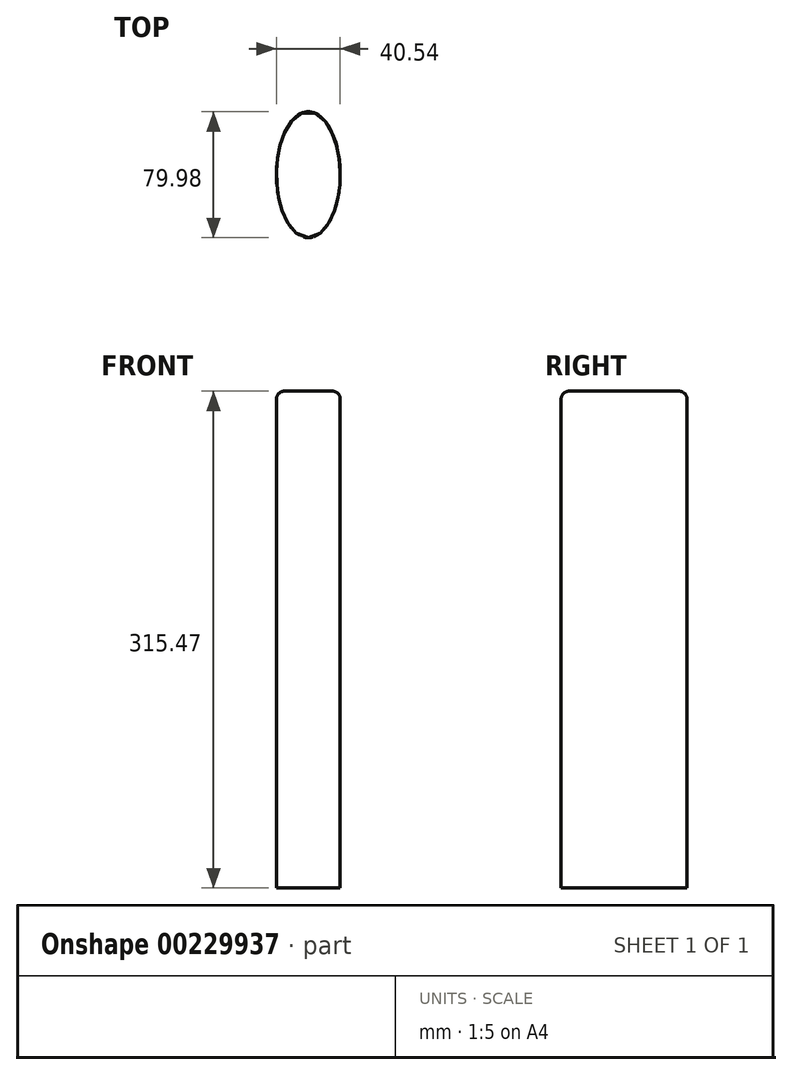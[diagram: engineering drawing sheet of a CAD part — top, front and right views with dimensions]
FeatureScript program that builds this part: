
annotation { "Feature Type Name" : "Feature", "Feature Type Description" : "" }
export const myFeature = defineFeature(function(context is Context, id is Id, definition is map)
    precondition{}
    {
        {
            var Q0;
            Q0=qCreatedBy(makeId("Top.planeOp"),FACE);
            var sketch = newSketch(context, id + "F0", { "sketchPlane" : qUnion([Q0])});
            skEllipse(sketch, "E0", {"center": v(0, 26.92) * mm, "majorRadius": 39.99 * mm, "minorRadius": 20.27 * mm, "majorAxis": v(0, -1)});
            skSolve(sketch);
        }
        {
            var Q0;
            Q0 = qSketchRegion(id + "F0", true);
            extrude(context, id + "F1", {"entities" : qUnion([Q0]), "depth" : 25.4 * mm});
        }
        {
            var Q0;
            Q0=makeQuery(id+"F1.opExtrude","CAP_FACE",FACE,{"disambiguationData":[OSD([sQuery(id+"F0.wireOp",EDGE,"E0")])],"isStart":false});
            var Q1;
            Q1=makeQuery(id+"F1.opExtrude","CAP_FACE",FACE,{"disambiguationData":[OSD([sQuery(id+"F0.wireOp",EDGE,"E0")])],"isStart":true});
            extrude(context, id + "F2", {"entities" : qUnion([Q0, Q1]), "operationType" : NewBodyOperationType.ADD, "depth" : 114.05 * mm});
        }
        {
            var Q0;
            Q0=makeQuery(id+"F1.opExtrude","CAP_FACE",FACE,{"disambiguationData":[OSD([sQuery(id+"F0.wireOp",EDGE,"E0")])],"isStart":true});
            extrude(context, id + "F3", {"entities" : qUnion([Q0]), "operationType" : NewBodyOperationType.ADD, "depth" : 25.4 * mm});
        }
        {
            var Q0;
            Q0=makeQuery(id+"F3.opExtrude","CAP_FACE",FACE,{"disambiguationData":[OSD([sQuery(id+"F0.wireOp",EDGE,"E0")])],"isStart":false});
            extrude(context, id + "F4", {"entities" : qUnion([Q0]), "operationType" : NewBodyOperationType.ADD, "depth" : 150.62 * mm});
        }
        {
            var Q0;
            {var subQ0=sQuery(id+"F0.wireOp",EDGE,"E0");Q0=makeQuery(id+"F2.opExtrude","CAP_EDGE",EDGE,{"disambiguationData":[OSD([subQ0]),TDD([makeQuery(id+"F1.opExtrude","CAP_EDGE",EDGE,{"disambiguationData":[OSD([subQ0])],"isStart":false})])],"isStart":false});}
            fillet(context, id + "F5", {"entities" : qUnion([Q0]), "radius" : 5.08 * mm, "tangentPropagation" : true, "allowEdgeOverflow" : false});
        }
    });
